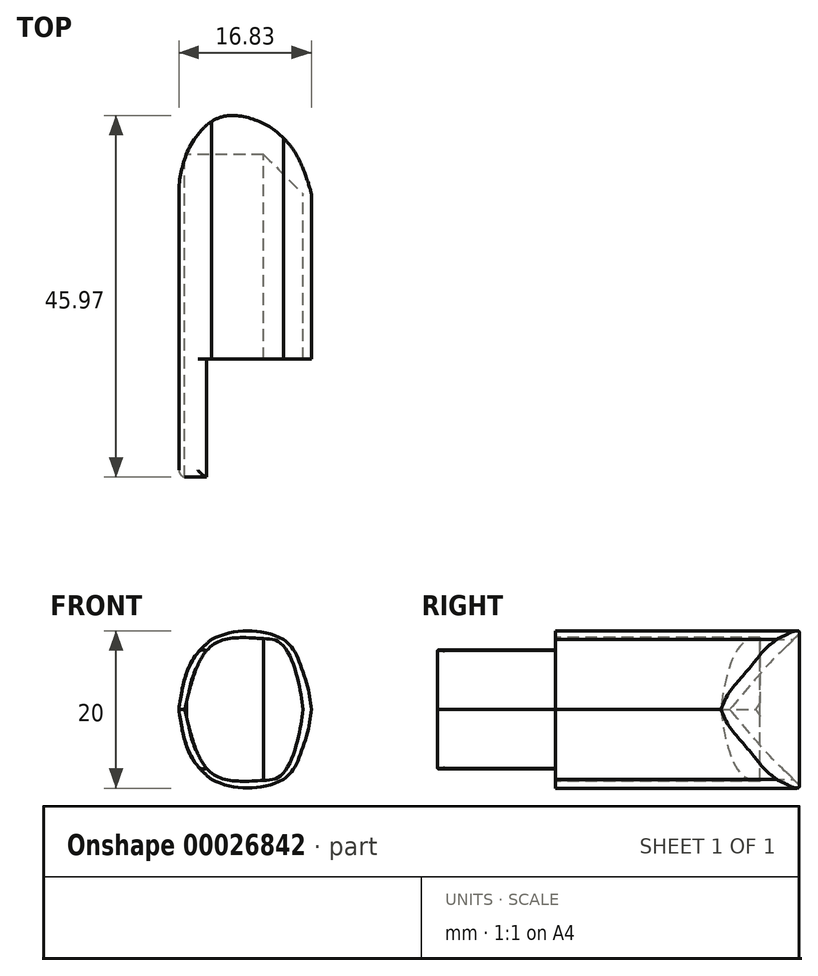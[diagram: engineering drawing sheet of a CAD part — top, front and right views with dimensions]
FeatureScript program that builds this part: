
annotation { "Feature Type Name" : "Feature", "Feature Type Description" : "" }
export const myFeature = defineFeature(function(context is Context, id is Id, definition is map)
    precondition{}
    {
        {
            var Q0;
            Q0=qCreatedBy(makeId("Front.planeOp"),FACE);
            var sketch = newSketch(context, id + "F0", { "sketchPlane" : qUnion([Q0])});
            skLineSegment(sketch, "E0", {"start": v(-10, 0) * mm, "end": v(5, 0) * mm});
            skLineSegment(sketch, "E1", {"start": v(0, 0) * mm, "end": v(0, -9) * mm});
            skLineSegment(sketch, "E2.MirrorCS", {"start": v(0, 0) * mm, "end": v(0, 9) * mm});
            skFitSpline(sketch, "E3", {"points": [v(5, 0) * mm, v(4.3, 4.1) * mm, v(2.22, 8.4) * mm, v(0, 9) * mm], "startDerivative": vector(-1.33, 10.89) * mm, "endDerivative": vector(-8.85, 0.3) * mm});
            skFitSpline(sketch, "E4.MirrorCS", {"points": [v(5, 0) * mm, v(4.3, -4.1) * mm, v(2.22, -8.4) * mm, v(0, -9) * mm], "startDerivative": vector(-1.33, -10.89) * mm, "endDerivative": vector(-8.85, -0.3) * mm});
            skFitSpline(sketch, "E5", {"points": [v(0, 9) * mm, v(-6.57, 8.1) * mm, v(-10, 0) * mm], "startDerivative": vector(-15.93, 1.14) * mm, "endDerivative": vector(-4.35, -18.67) * mm});
            skFitSpline(sketch, "E6.MirrorCS", {"points": [v(0, -9) * mm, v(-6.57, -8.1) * mm, v(-10, 0) * mm], "startDerivative": vector(-15.93, -1.14) * mm, "endDerivative": vector(-4.35, 18.67) * mm});
            skSolve(sketch);
        }
        {
            var Q0;
            Q0=qCreatedBy(makeId("Front.planeOp"),FACE);
            var sketch = newSketch(context, id + "F1", { "sketchPlane" : qUnion([Q0])});
            skLineSegment(sketch, "E7", {"start": v(0, 0) * mm, "end": v(-2, 0) * mm});
            skCircle(sketch, "E8", {"center": v(-2, 0) * mm, "radius": 10 * mm});
            skFitSpline(sketch, "E9", {"points": [v(-10.74, 0) * mm, v(-9.99, 3.97) * mm, v(-8.53, 7) * mm, v(-6.6, 8.88) * mm], "startDerivative": vector(1.56, 11.12) * mm, "endDerivative": vector(6.83, 5.68) * mm});
            skFitSpline(sketch, "E10.MirrorCS", {"points": [v(-10.74, 0) * mm, v(-9.99, -3.97) * mm, v(-8.53, -7) * mm, v(-6.6, -8.88) * mm], "startDerivative": vector(1.56, -11.12) * mm, "endDerivative": vector(6.83, -5.68) * mm});
            skFitSpline(sketch, "E11", {"points": [v(6.1, 0) * mm, v(5.73, 2.4) * mm, v(4.83, 5.27) * mm, v(3.75, 7.68) * mm, v(2.54, 8.91) * mm], "startDerivative": vector(-1.05, 9.38) * mm, "endDerivative": vector(-6.12, 5.07) * mm});
            skFitSpline(sketch, "E12.MirrorCS", {"points": [v(6.1, 0) * mm, v(5.73, -2.4) * mm, v(4.83, -5.27) * mm, v(3.75, -7.68) * mm, v(2.54, -8.91) * mm], "startDerivative": vector(-1.05, -9.38) * mm, "endDerivative": vector(-6.12, -5.07) * mm});
            skSolve(sketch);
        }
        {
            var Q0;
            {var subQ2=sQuery(id+"F1.wireOp",EDGE,"E9");Q0=makeQuery(id+"F1.imprint","IMPRINT",FACE,{"disambiguationData":[TD([[makeQuery(id+"F1.imprint","IMPRINT",EDGE,{"derivedFrom":subQ2}),-1.0]])]});}
            extrude(context, id + "F2", {"entities" : qUnion([Q0]), "depth" : 26 * mm});
        }
        {
            var Q0;
            {var subQ1=sQuery(id+"F0.wireOp",EDGE,"E2.MirrorCS");Q0=makeQuery(id+"F0.imprint","IMPRINT",FACE,{"disambiguationData":[TD([[makeQuery(id+"F0.imprint","IMPRINT",EDGE,{"derivedFrom":subQ1}),-1.0]])]});}
            var Q1;
            {var subQ1=sQuery(id+"F0.wireOp",EDGE,"E2.MirrorCS");Q1=makeQuery(id+"F0.imprint","IMPRINT",FACE,{"disambiguationData":[TD([[makeQuery(id+"F0.imprint","IMPRINT",EDGE,{"derivedFrom":subQ1}),1.0]])]});}
            var Q2;
            {var subQ1=sQuery(id+"F0.wireOp",EDGE,"E1");Q2=makeQuery(id+"F0.imprint","IMPRINT",FACE,{"disambiguationData":[TD([[makeQuery(id+"F0.imprint","IMPRINT",EDGE,{"derivedFrom":subQ1}),1.0]])]});}
            var Q3;
            {var subQ0=sQuery(id+"F0.wireOp",EDGE,"E1");Q3=makeQuery(id+"F0.imprint","IMPRINT",FACE,{"disambiguationData":[TD([[makeQuery(id+"F0.imprint","IMPRINT",EDGE,{"derivedFrom":subQ0}),-1.0]])]});}
            extrude(context, id + "F3", {"entities" : qUnion([Q0, Q1, Q2, Q3]), "operationType" : NewBodyOperationType.REMOVE, "depth" : 26 * mm});
        }
        {
            var Q0;
            {var subQ1=sQuery(id+"F0.wireOp",EDGE,"E2.MirrorCS");Q0=makeQuery(id+"F0.imprint","IMPRINT",FACE,{"disambiguationData":[TD([[makeQuery(id+"F0.imprint","IMPRINT",EDGE,{"derivedFrom":subQ1}),-1.0]])]});}
            var Q1;
            {var subQ1=sQuery(id+"F0.wireOp",EDGE,"E1");Q1=makeQuery(id+"F0.imprint","IMPRINT",FACE,{"disambiguationData":[TD([[makeQuery(id+"F0.imprint","IMPRINT",EDGE,{"derivedFrom":subQ1}),1.0]])]});}
            extrude(context, id + "F4", {"entities" : qUnion([Q0, Q1]), "operationType" : NewBodyOperationType.ADD, "depth" : 8 * mm});
        }
        {
            var Q0;
            Q0=makeQuery(id+"F4.opExtrude","CAP_EDGE",EDGE,{"disambiguationData":[OSD([sQuery(id+"F0.wireOp",EDGE,"E1"),sQuery(id+"F0.wireOp",EDGE,"E2.MirrorCS")])],"isStart":false});
            chamfer(context, id + "F5", {"entities" : qUnion([Q0]), "width" : 8 * mm, "tangentPropagation" : true});
        }
        {
            var Q0;
            {var subQ2=sQuery(id+"F1.wireOp",EDGE,"E9");Q0=makeQuery(id+"F1.imprint","IMPRINT",FACE,{"disambiguationData":[TD([[makeQuery(id+"F1.imprint","IMPRINT",EDGE,{"derivedFrom":subQ2}),-1.0]])]});}
            extrude(context, id + "F6", {"entities" : qUnion([Q0]), "operationType" : NewBodyOperationType.ADD, "oppositeDirection" : true, "depth" : 5 * mm});
        }
        {
            var Q0;
            Q0=qCreatedBy(makeId("Top.planeOp"),FACE);
            var sketch = newSketch(context, id + "F7", { "sketchPlane" : qUnion([Q0])});
            skFitSpline(sketch, "E13", {"points": [v(6.98, -8.91) * mm, v(5.59, -3.32) * mm, v(2.74, 2.41) * mm, v(-1.22, 6.74) * mm], "startDerivative": vector(-3.49, 17.01) * mm, "endDerivative": vector(-12.75, 12.23) * mm});
            skLineSegment(sketch, "E14", {"start": v(-1.22, 6.74) * mm, "end": v(9.15, 6.74) * mm});
            skLineSegment(sketch, "E15", {"start": v(9.15, 6.74) * mm, "end": v(9.15, -9.12) * mm});
            skLineSegment(sketch, "E16", {"start": v(9.15, -9.12) * mm, "end": v(6.98, -8.91) * mm});
            skSolve(sketch);
        }
        {
            var Q0;
            Q0=makeQuery(id+"F7.imprint","IMPRINT",FACE,{"disambiguationData":[TD([[makeQuery(id+"F7.imprint","IMPRINT",EDGE,{"derivedFrom":sQuery(id+"F7.wireOp",EDGE,"E13")}),-1.0]])]});
            extrude(context, id + "F8", {"entities" : qUnion([Q0]), "operationType" : NewBodyOperationType.REMOVE, "endBound" : BoundingType.SYMMETRIC, "oppositeDirection" : true, "depth" : 40 * mm});
        }
        {
            var Q0;
            Q0=makeQuery(id+"F8.boolean.opBoolean","INTERSECT",EDGE,{"derivedFrom":[makeQuery(id+"F6.opExtrude","CAP_FACE",FACE,{"disambiguationData":[OSD([sQuery(id+"F1.wireOp",EDGE,"E8"),sQuery(id+"F1.wireOp",EDGE,"E9"),sQuery(id+"F1.wireOp",EDGE,"E10.MirrorCS"),sQuery(id+"F1.wireOp",EDGE,"E11"),sQuery(id+"F1.wireOp",EDGE,"E12.MirrorCS")])],"isStart":false}),makeQuery(id+"F8.opExtrude","SWEPT_FACE",FACE,{"disambiguationData":[OSD([sQuery(id+"F7.wireOp",EDGE,"E13")])]})]});
            fillet(context, id + "F9", {"entities" : qUnion([Q0]), "radius" : 10 * mm, "tangentPropagation" : true, "allowEdgeOverflow" : false});
        }
        {
            var Q0;
            Q0=qCreatedBy(makeId("Top.planeOp"),FACE);
            var sketch = newSketch(context, id + "F10", { "sketchPlane" : qUnion([Q0])});
            skFitSpline(sketch, "E17", {"points": [v(-2.66, 7.57) * mm, v(-5.85, 4.98) * mm, v(-9.8, 0) * mm, v(-12.18, -12.29) * mm], "startDerivative": vector(-11.9, -10.68) * mm, "endDerivative": vector(-8.62, -30.34) * mm});
            skLineSegment(sketch, "E18", {"start": v(-2.66, 7.57) * mm, "end": v(-12.7, 7.57) * mm});
            skLineSegment(sketch, "E19", {"start": v(-12.7, 7.57) * mm, "end": v(-12.18, -12.29) * mm});
            skSolve(sketch);
        }
        {
            var Q0;
            Q0=makeQuery(id+"F10.imprint","IMPRINT",FACE,{"disambiguationData":[TD([[makeQuery(id+"F10.imprint","IMPRINT",EDGE,{"derivedFrom":sQuery(id+"F10.wireOp",EDGE,"E17")}),-1.0]])]});
            extrude(context, id + "F11", {"entities" : qUnion([Q0]), "operationType" : NewBodyOperationType.REMOVE, "endBound" : BoundingType.SYMMETRIC, "oppositeDirection" : true, "depth" : 25 * mm});
        }
        {
            var Q0;
            Q0=makeQuery(id+"F11.boolean.opBoolean","INTERSECT",EDGE,{"derivedFrom":[makeQuery(id+"F6.opExtrude","CAP_FACE",FACE,{"disambiguationData":[OSD([sQuery(id+"F1.wireOp",EDGE,"E8"),sQuery(id+"F1.wireOp",EDGE,"E9"),sQuery(id+"F1.wireOp",EDGE,"E10.MirrorCS"),sQuery(id+"F1.wireOp",EDGE,"E11"),sQuery(id+"F1.wireOp",EDGE,"E12.MirrorCS")])],"isStart":false}),makeQuery(id+"F11.opExtrude","SWEPT_FACE",FACE,{"disambiguationData":[OSD([sQuery(id+"F10.wireOp",EDGE,"E17")])]})]});
            fillet(context, id + "F12", {"entities" : qUnion([Q0]), "radius" : 5 * mm, "tangentPropagation" : true, "allowEdgeOverflow" : false});
        }
        {
            var Q0;
            Q0=makeQuery(id+"F2.opExtrude","CAP_FACE",FACE,{"disambiguationData":[OSD([sQuery(id+"F1.wireOp",EDGE,"E8"),sQuery(id+"F1.wireOp",EDGE,"E9"),sQuery(id+"F1.wireOp",EDGE,"E10.MirrorCS"),sQuery(id+"F1.wireOp",EDGE,"E11"),sQuery(id+"F1.wireOp",EDGE,"E12.MirrorCS")])],"isStart":false});
            var sketch = newSketch(context, id + "F13", { "sketchPlane" : qUnion([Q0])});
            skLineSegment(sketch, "E20", {"start": v(-7.22, -8.35) * mm, "end": v(-7.22, -7.48) * mm});
            skLineSegment(sketch, "E21.MirrorCS", {"start": v(-7.22, 8.35) * mm, "end": v(-7.22, 7.48) * mm});
            skSolve(sketch);
        }
        {
            var Q0;
            {var subQ1=sQuery(id+"F13.wireOp",EDGE,"E20");Q0=makeQuery(id+"F13.imprint","IMPRINT",FACE,{"disambiguationData":[TD([[makeQuery(id+"F13.imprint","IMPRINT",EDGE,{"derivedFrom":subQ1}),1.0]])]});}
            extrude(context, id + "F14", {"entities" : qUnion([Q0]), "operationType" : NewBodyOperationType.ADD, "depth" : 15 * mm});
        }
        {
            var Q0;
            Q0=makeQuery(id+"F14.opExtrude","SWEPT_EDGE",EDGE,{"disambiguationData":[OSD([sQuery(id+"F1.wireOp",EDGE,"E10.MirrorCS"),sQuery(id+"F13.wireOp",EDGE,"E20")])]});
            var Q1;
            Q1=makeQuery(id+"F14.opExtrude","CAP_EDGE",EDGE,{"disambiguationData":[OSD([sQuery(id+"F1.wireOp",EDGE,"E10.MirrorCS")])],"isStart":false});
            var Q2;
            Q2=makeQuery(id+"F14.opExtrude","CAP_EDGE",EDGE,{"disambiguationData":[OSD([sQuery(id+"F1.wireOp",EDGE,"E9")])],"isStart":false});
            var Q3;
            Q3=makeQuery(id+"F14.opExtrude","SWEPT_EDGE",EDGE,{"disambiguationData":[OSD([sQuery(id+"F1.wireOp",EDGE,"E9"),sQuery(id+"F13.wireOp",EDGE,"E21.MirrorCS")])]});
            fillet(context, id + "F15", {"entities" : qUnion([Q0, Q1, Q2, Q3]), "radius" : 0.9 * mm, "tangentPropagation" : true, "allowEdgeOverflow" : false});
        }
    });
